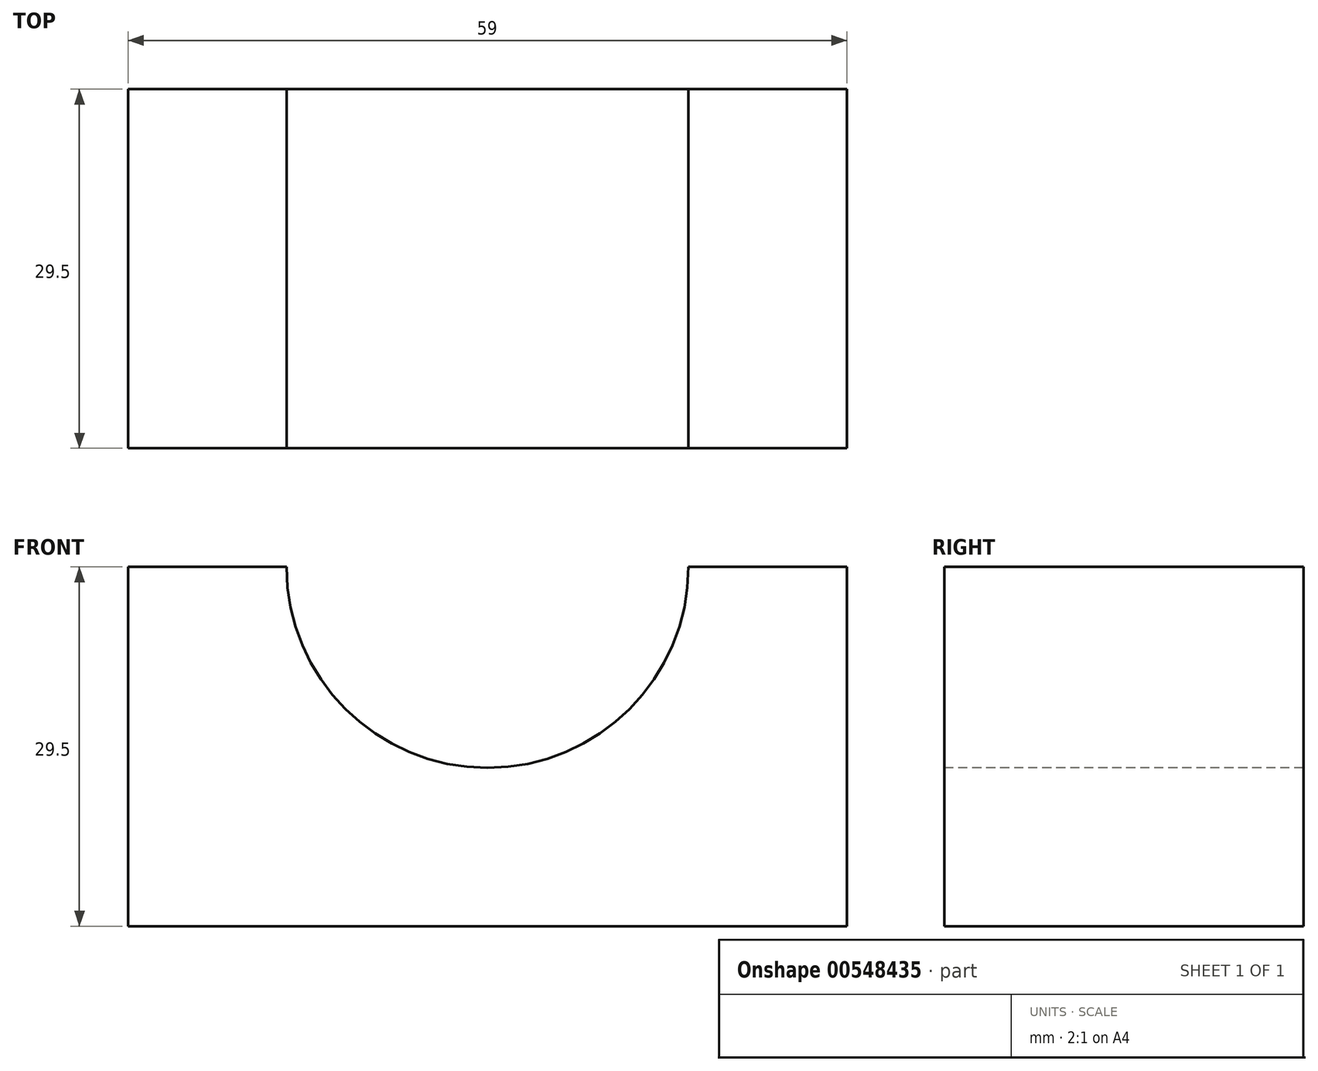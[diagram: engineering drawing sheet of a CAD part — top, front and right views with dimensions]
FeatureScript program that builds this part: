
annotation { "Feature Type Name" : "Feature", "Feature Type Description" : "" }
export const myFeature = defineFeature(function(context is Context, id is Id, definition is map)
    precondition{}
    {
        {
            var Q0;
            Q0=qCreatedBy(makeId("Front.planeOp"),FACE);
            var sketch = newSketch(context, id + "F0", { "sketchPlane" : qUnion([Q0])});
            skLineSegment(sketch, "E0.bottom", {"start": v(29.5, 29.5) * mm, "end": v(-29.5, 29.5) * mm});
            skLineSegment(sketch, "E0.top", {"start": v(29.5, -29.5) * mm, "end": v(-29.5, -29.5) * mm});
            skLineSegment(sketch, "E0.left", {"start": v(29.5, 29.5) * mm, "end": v(29.5, -29.5) * mm});
            skLineSegment(sketch, "E0.right", {"start": v(-29.5, 29.5) * mm, "end": v(-29.5, -29.5) * mm});
            skPoint(sketch, "E0.middle", {"position": v(0, 0) * mm});
            skSolve(sketch);
        }
        {
            var Q0;
            Q0=makeQuery(id+"F0.imprint","IMPRINT",FACE,{"disambiguationData":[TD([[makeQuery(id+"F0.imprint","IMPRINT",EDGE,{"derivedFrom":sQuery(id+"F0.wireOp",EDGE,"E0.bottom")}),1.0]])]});
            extrude(context, id + "F1", {"entities" : qUnion([Q0]), "depth" : 29.5 * mm, "offsetDistance" : 25 * mm});
        }
        {
            var Q0;
            Q0=makeQuery(id+"F1.opExtrude","CAP_FACE",FACE,{"disambiguationData":[OSD([sQuery(id+"F0.wireOp",EDGE,"E0.bottom"),sQuery(id+"F0.wireOp",EDGE,"E0.top"),sQuery(id+"F0.wireOp",EDGE,"E0.left"),sQuery(id+"F0.wireOp",EDGE,"E0.right")])],"isStart":false});
            var sketch = newSketch(context, id + "F2", { "sketchPlane" : qUnion([Q0])});
            skCircle(sketch, "E1", {"center": v(0, 0) * mm, "radius": 16.5 * mm});
            skSolve(sketch);
        }
        {
            var Q0;
            Q0=makeQuery(id+"F2.imprint","IMPRINT",FACE,{"disambiguationData":[TD([[makeQuery(id+"F2.imprint","IMPRINT",EDGE,{"derivedFrom":sQuery(id+"F2.wireOp",EDGE,"E1")}),1.0]])]});
            extrude(context, id + "F3", {"entities" : qUnion([Q0]), "operationType" : NewBodyOperationType.REMOVE, "endBound" : BoundingType.THROUGH_ALL, "oppositeDirection" : true, "depth" : 25 * mm, "offsetDistance" : 25 * mm});
        }
        {
            var Q0;
            Q0=makeQuery(id+"F1.opExtrude","CAP_FACE",FACE,{"disambiguationData":[OSD([sQuery(id+"F0.wireOp",EDGE,"E0.bottom"),sQuery(id+"F0.wireOp",EDGE,"E0.top"),sQuery(id+"F0.wireOp",EDGE,"E0.left"),sQuery(id+"F0.wireOp",EDGE,"E0.right")])],"isStart":true});
            var sketch = newSketch(context, id + "F4", { "sketchPlane" : qUnion([Q0])});
            skLineSegment(sketch, "E2", {"start": v(-29.5, 29.5) * mm, "end": v(29.5, 29.5) * mm});
            skLineSegment(sketch, "E3", {"start": v(29.5, 29.5) * mm, "end": v(29.5, 0) * mm});
            skLineSegment(sketch, "E4", {"start": v(29.5, 0) * mm, "end": v(-29.5, 0) * mm});
            skLineSegment(sketch, "E5", {"start": v(-29.5, 0) * mm, "end": v(-29.5, 29.5) * mm});
            skSolve(sketch);
        }
        {
            var Q0;
            Q0 = qSketchRegion(id + "F4", true);
            extrude(context, id + "F5", {"entities" : qUnion([Q0]), "operationType" : NewBodyOperationType.REMOVE, "endBound" : BoundingType.THROUGH_ALL, "oppositeDirection" : true, "depth" : 25 * mm, "offsetDistance" : 25 * mm});
        }
    });
